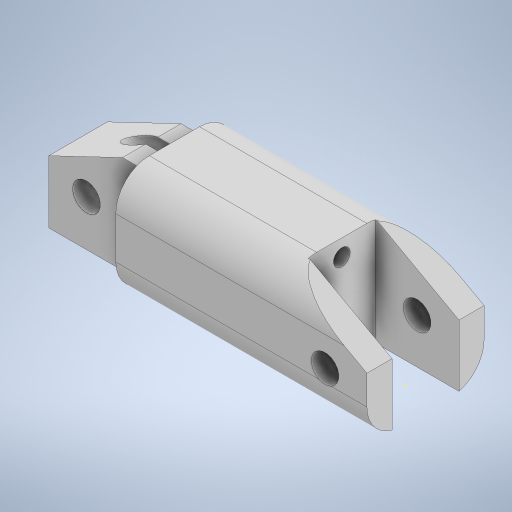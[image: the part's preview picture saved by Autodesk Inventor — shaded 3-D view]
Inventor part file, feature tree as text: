
AUTODESK INVENTOR PART (.ipt)
format: ipt  version: 2024 (Build 280153000, 153)  size: 578,560 bytes
history: native  units: mm
features: sketch x30, extrude x26, move_body x5, chamfer x3, plane x3, split x3, boolean_combine x3, other x1, fillet x1, imported_body x1
ambient origin geometry x8: Origin, YZ Plane, XZ Plane, XY Plane, X Axis, Y Axis, Z Axis, Center Point
bodies: Solid1 (feature_tree), Solid2 (feature_tree), Solid3 (feature_tree), Solid6 (feature_tree), Solid7 (feature_tree), Solid8 (feature_tree), Solid9 (feature_tree), Solid12 (feature_tree)
feature tree (76):
  other  "Repaired Geometry1"
  extrude  "Extrusion1"  Depth=16.0mm
  sketch  "Sketch2"  dims[d2=15.0mm d3=0.0mm d4=10.0mm]
  extrude  "Extrusion2"  Depth=10.0mm
  chamfer  "Chamfer1"  Distance=21.25mm
  extrude  "Extrusion3"  Depth=10.0mm TaperAngle=0.0deg
  extrude  "Extrusion4"  Depth=11.5mm TaperAngle=0.0deg
  extrude  "Extrusion5"  Depth=11.5mm TaperAngle=0.0deg
  chamfer  "Chamfer2"  Distance=11.5mm Angle=45.0deg
  sketch  "Sketch6"  dims[d14=7.0mm d15=11.5mm d16=0.0mm]
  extrude  "Extrusion6"  Depth=9.0mm
  extrude  "Extrusion7"  Depth=11.5mm TaperAngle=0.0deg
  chamfer  "Chamfer3"  Distance=11.5mm Angle=45.0deg
  sketch  "Sketch9"  dims[d26=3.3mm d27=45.25mm d28=0.0mm d29=11.5mm d30=5.5mm d31=45.0deg]
  extrude  "Extrusion8"  Depth=65.75mm TaperAngle=0.0deg
  extrude  "Extrusion9"  Depth=9.0mm TaperAngle=0.0deg
  extrude  "Extrusion10"  Depth=13.0mm TaperAngle=0.0deg
  sketch  "Sketch13"  dims[d43=24.0mm d44=21.0mm d45=0.0mm]
  extrude  "Extrusion11"  Depth=24.0mm TaperAngle=0.0deg
  extrude  "Extrusion12"  TaperAngle=0.0deg  [1 undecoded]
  extrude  "Extrusion13"  Depth=6.0mm TaperAngle=0.0deg
  plane  "Work Plane1"
  split  "Split1"
  move_body  "Move Body1"
  extrude  "Extrusion14"  Depth=0.5mm TaperAngle=0.0deg
  move_body  "Move Body2"
  extrude  "Extrusion15"  Depth=10.0mm
  sketch  "Sketch19"  dims[d70=31.0mm d71=29.5mm d72=0.0mm]
  sketch  "Sketch20"  dims[d74=11.0mm d75=1.0mm]
  extrude  "Extrusion16"  Depth=10.0mm
  extrude  "Extrusion18"  Depth=29.5mm TaperAngle=0.0deg
  extrude  "Extrusion19"  Depth=1.0mm
  extrude  "Extrusion20"  Depth=10.0mm TaperAngle=0.0deg
  boolean_combine  "Combine1"
  plane  "Work Plane3"
  split  "Split3"
  extrude  "Extrusion21"  TaperAngle=0.0deg  [1 undecoded]
  plane  "Work Plane4"
  split  "Split4"
  move_body  "Move Body3"
  move_body  "Move Body4"
  boolean_combine  "Combine3"
  extrude  "Extrusion22"  Depth=1.0mm TaperAngle=0.0deg
  extrude  "Extrusion23"  Depth=12.5mm TaperAngle=0.0deg
  extrude  "Extrusion24"  TaperAngle=0.0deg  [1 undecoded]
  extrude  "Extrusion25"  Depth=46.5mm TaperAngle=0.0deg
  move_body  "Move Body5"
  sketch  "Sketch32"  dims[d102=46.5mm d103=0.0mm d104=4.0mm]
  boolean_combine  "Combine4"
  extrude  "Extrusion26"  Depth=2.0mm
  extrude  "Extrusion27"  Depth=4.0mm
  fillet  "Fillet2"  [1 undecoded]
  sketch  "Sketch34"
  sketch  "Sketch1"  dims[d0=36.0mm d1=16.0mm]
  sketch  "Sketch3"  dims[d5=10.0mm]
  sketch  "Sketch4"  dims[d6=3.3mm d7=21.25mm d8=0.0mm]
  sketch  "Sketch5"  dims[d9=10.0mm d10=5.5mm d11=45.0deg d12=10.0mm d13=0.0mm]
  sketch  "Sketch7"  dims[d17=3.3mm d18=1.0mm d19=0.0mm d20=6.0mm d21=11.5mm d22=45.0deg]
  sketch  "Sketch8"  dims[d23=15.0mm d24=0.0mm d25=9.0mm]
  sketch  "Sketch10"  dims[d32=2.0mm d33=65.75mm d34=0.0mm]
  sketch  "Sketch11"  dims[d35=0.5mm d36=0.0mm d37=9.0mm d38=0.0mm]
  sketch  "Sketch12"  dims[d39=0.5mm d40=0.0mm d41=13.0mm d42=0.0mm]
  sketch  "Sketch14"  dims[d46=12.25mm d47=-12.0mm d48=0.0mm d49=0.0mm]
  sketch  "Sketch15"  dims[d50=30.0mm d51=0.0mm d52=6.0mm d53=0.0mm d54=0.0mm]
  sketch  "Sketch16"  dims[d56=0.5mm d57=0.0mm d58=0.5mm d59=0.0mm]
  sketch  "Sketch17"  dims[d64=10.0mm d65=0.0mm d66=3.0mm]
  sketch  "Sketch18"  dims[d67=10.0mm d68=0.0mm d69=1.0mm]
  sketch  "Sketch22"  dims[d76=1.0mm d77=10.0mm d78=0.0mm]
  sketch  "Sketch25"  dims[d79=5.5mm d80=0.0mm d81=0.0mm d82=-1.0mm]
  sketch  "Sketch27"  dims[d83=0.0mm d84=0.0mm d85=1.0mm d86=1.0mm d87=0.0mm]
  sketch  "Sketch28"  dims[d88=1.0mm d89=0.0mm d90=12.5mm d91=0.0mm]
  sketch  "Sketch29"  dims[d92=19.0mm d93=0.0mm d94=-12.0mm d95=0.0mm d96=0.0mm]
  sketch  "Sketch30"  dims[d97=2.0mm d98=46.5mm d99=0.0mm]
  sketch  "Sketch31"  dims[d100=2.0mm d101=2.0mm]
  sketch  "Sketch33"
  imported_body  "Base1"
note: 4 required parameter values undecoded (feature->parameter linkage not recoverable at this tier; creation-order binding heuristic only, values carry confidence <= 0.55)
